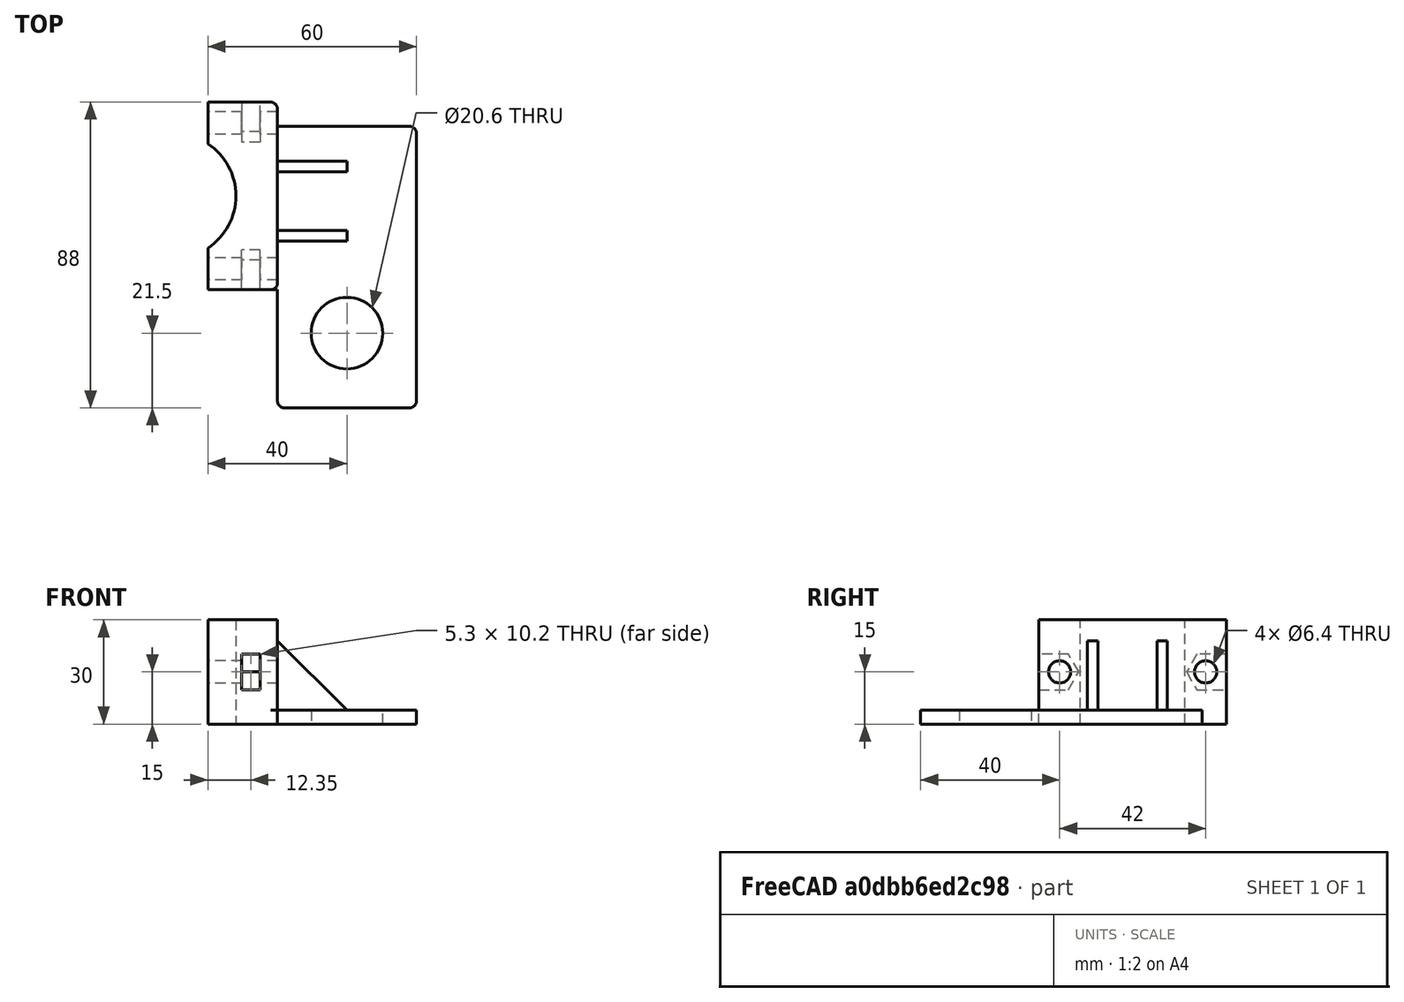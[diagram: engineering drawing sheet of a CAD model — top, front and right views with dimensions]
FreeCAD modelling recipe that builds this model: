
FCSTD DOCUMENT  (FreeCAD 0.18R16117 (Git))
Label: encloser_halter_v2
License: All rights reserved
LicenseURL: http://en.wikipedia.org/wiki/All_rights_reserved
objects: TechDraw::DrawViewDimension×8, Sketcher::SketchObject×4, Part::Extrusion×4, Part::FeaturePython×3, TechDraw::DrawProjGroupItem×3, Part::MultiFuse×2, Part::Cylinder×1, Part::Fillet×1, Part::Cut×1, TechDraw::DrawSVGTemplate×1, TechDraw::DrawProjGroup×1, TechDraw::DrawPage×1
note: 16 computed .brp shape members not serialized (recipe doc carries the construction recipe); baked Part::Feature solids carry a one-line shape summary decoded from their .brp

FEATURE [Sketcher::SketchObject] Sketch
  sketch-geometry (9):
    g0: LineSegment StartX=38 StartY=0 StartZ=0 EndX=2 EndY=0 EndZ=0
    g1: LineSegment StartX=0 StartY=2 StartZ=0 EndX=0 EndY=81 EndZ=0
    g2: LineSegment StartX=0 StartY=81 StartZ=0 EndX=38 EndY=81 EndZ=0
    g3: LineSegment StartX=40 StartY=79 StartZ=0 EndX=40 EndY=2 EndZ=0
    g4: Circle CenterX=20 CenterY=21.5 CenterZ=0 NormalX=0 NormalY=0 NormalZ=1 AngleXU=0 Radius=10.3
    g5: LineSegment [constr] StartX=20 StartY=0 StartZ=0 EndX=20 EndY=81 EndZ=0
    g6: ArcOfCircle CenterX=38 CenterY=79 CenterZ=0 NormalX=0 NormalY=0 NormalZ=1 AngleXU=0 Radius=2 StartAngle=-9e-16 EndAngle=1.5708
    g7: ArcOfCircle CenterX=38 CenterY=2 CenterZ=0 NormalX=0 NormalY=0 NormalZ=1 AngleXU=0 Radius=2 StartAngle=4.71239 EndAngle=6.28319
    g8: ArcOfCircle CenterX=2 CenterY=2 CenterZ=0 NormalX=0 NormalY=0 NormalZ=1 AngleXU=0 Radius=2 StartAngle=3.14159 EndAngle=4.71239
  constraints (24):
    c: Coincident(g1,g2)
    c: Horizontal(g0)
    c: Horizontal(g2)
    c: Vertical(g1)
    c: Vertical(g3)
    c: Radius(g4) = 10.3
    c: PointOnObject(g5,g0)
    c: PointOnObject(g4,g5)
    c: DistanceY(g-1,g4) = 21.5
    c: PointOnObject(g5,g2)
    c: Tangent(g2,g6) = 1.5708
    c: Tangent(g3,g6) = 1.5708
    c: Tangent(g3,g7) = 1.5708
    c: Tangent(g0,g7) = 1.5708
    c: Tangent(g1,g8) = 1.5708
    c: Tangent(g0,g8) = 1.5708
    c: Radius(g8) = 2
    c: Equal(g8,g7)
    c: Equal(g8,g6)
    c: DistanceX(g1,g3) = 40
    c: PointOnObject(g1,g-2)
    c: PointOnObject(g0,g-1)
    c: DistanceY(g0,g2) = 81
    c: Symmetric(g1,g3,g5)
FEATURE [Part::Extrusion] Extrude  label="encloser_mount_plate"
  Base = -> Sketch
  Dir = (0,0,1)
  DirMode = 2
  FaceMakerClass = Part::FaceMakerBullseye
  LengthFwd = 4
  LengthRev = 0
  Placement = pos=(0,-61,0) rot=(0,0,1;0rad)
  Solid = true
  Symmetric = false
FEATURE [Sketcher::SketchObject] Sketch002  label="Sketch_encloser_mastbefestigung"
  sketch-geometry (6):
    g0: LineSegment StartX=-20 StartY=27 StartZ=0 EndX=0 EndY=27 EndZ=0
    g1: LineSegment StartX=0 StartY=27 StartZ=0 EndX=0 EndY=-27 EndZ=0
    g2: LineSegment StartX=0 StartY=-27 StartZ=0 EndX=-20 EndY=-27 EndZ=0
    g3: LineSegment StartX=-20 StartY=-27 StartZ=0 EndX=-20 EndY=-15 EndZ=0
    g4: LineSegment StartX=-20 StartY=15 StartZ=0 EndX=-20 EndY=27 EndZ=0
    g5: ArcOfCircle CenterX=-29.9499 CenterY=2e-16 CenterZ=0 NormalX=0 NormalY=0 NormalZ=1 AngleXU=0 Radius=18 StartAngle=5.29807 EndAngle=7.2683
  constraints (17):
    c: Horizontal(g0)
    c: Horizontal(g2)
    c: Coincident(g2,g3)
    c: Vertical(g3)
    c: Coincident(g4,g0)
    c: Vertical(g4)
    c: Coincident(g5,g4)
    c: Coincident(g5,g3)
    c: DistanceY(g3,g3) = 12
    c: Symmetric(g3,g4,g-1)
    c: DistanceY(g2,g0) = 54
    c: PointOnObject(g1,g-2)
    c: DistanceX(g2,g1) = 20
    c: Symmetric(g2,g0,g-1)
    c: Coincident(g0,g1)
    c: Coincident(g2,g1)
    c: Radius(g5) = 18
FEATURE [Part::Extrusion] Extrude002  label="encloser_mastbefestigung"
  Base = -> Sketch002
  Dir = (0,0,1)
  DirMode = 2
  FaceMakerClass = Part::FaceMakerBullseye
  LengthFwd = 30
  LengthRev = 0
  Solid = true
  Symmetric = false
FEATURE [Part::Cylinder] Cylinder  label="Bohrung"
  Angle = 360
  AttacherType = Attacher::AttachEngine3D
  Height = 30
  Placement = pos=(0,-21,15) rot=(0,-1,0;1.5708rad)
  Radius = 3.2
FEATURE [Part::FeaturePython] Clone  label="Bohrung001"  # Draft clone (typed FeaturePython)
  AttacherType = Attacher::AttachEngine3D
  Fuse = false
  Objects = -> [Cylinder]
  Placement = pos=(0,21,15) rot=(0,-1,0;1.5708rad)
  Scale = (1,1,1)
FEATURE [Sketcher::SketchObject] Sketch003  label="Sketch_Winkel"
  ExternalGeometry = -> [Extrude002,Extrude]
  Placement = pos=(0,0,0) rot=(1,0,0;1.5708rad)
  sketch-geometry (3):
    g0: LineSegment StartX=0 StartY=24 StartZ=0 EndX=20 EndY=4 EndZ=0
    g1: LineSegment StartX=20 StartY=4 StartZ=0 EndX=0 EndY=4 EndZ=0
    g2: LineSegment StartX=0 StartY=4 StartZ=0 EndX=0 EndY=24 EndZ=0
  constraints (9):
    c: PointOnObject(g0,g-3)
    c: PointOnObject(g0,g-4)
    c: Coincident(g0,g1)
    c: PointOnObject(g1,g-3)
    c: Horizontal(g1)
    c: Coincident(g1,g2)
    c: Coincident(g2,g0)
    c: DistanceX(g1,g1) = 20
    c: DistanceY(g2,g2) = 20
FEATURE [Part::Extrusion] Extrude003  label="Winkel"
  Base = -> Sketch003
  Dir = (0,-1,2e-16)
  DirMode = 2
  FaceMakerClass = Part::FaceMakerBullseye
  LengthFwd = 3
  LengthRev = 0
  Placement = pos=(0,-10,0) rot=(0,0,1;0rad)
  Solid = true
  Symmetric = false
FEATURE [Part::FeaturePython] Clone001  label="Winkel001"  # Draft clone (typed FeaturePython)
  AttacherType = Attacher::AttachEngine3D
  Fuse = false
  Objects = -> [Extrude003]
  Placement = pos=(0,10,0) rot=(0,0,1;0rad)
  Scale = (1,1,1)
FEATURE [Part::MultiFuse] Fusion001  label="encloser_halter_roh"
  Shapes = -> [Extrude,Extrude002,Extrude003,Clone001]
FEATURE [Part::Fillet] Fillet  label="encloser_halter_gerundet"
  Base = -> Fusion001
  Edges = 2 edges r=2: [Edge48,Edge50]
FEATURE [Sketcher::SketchObject] Sketch004  label="Sketch_Ausschnitt_M6"
  Placement = pos=(0,0,0) rot=(0.57735,-0.57735,-0.57735;2.0944rad)
  sketch-geometry (6):
    g0: LineSegment StartX=15.5 StartY=15 StartZ=0 EndX=18.4445 EndY=20.1 EndZ=0
    g1: LineSegment StartX=18.4445 StartY=20.1 StartZ=0 EndX=30.4445 EndY=20.1 EndZ=0
    g2: LineSegment StartX=30.4445 StartY=20.1 StartZ=0 EndX=30.4445 EndY=9.9 EndZ=0
    g3: LineSegment StartX=30.4445 StartY=9.9 StartZ=0 EndX=18.4445 EndY=9.9 EndZ=0
    g4: LineSegment StartX=18.4445 StartY=9.9 StartZ=0 EndX=15.5 EndY=15 EndZ=0
    g5: LineSegment [constr] StartX=30.4445 StartY=15 StartZ=0 EndX=15.5 EndY=15 EndZ=0
  constraints (14):
    c: Coincident(g0,g1)
    c: Horizontal(g1)
    c: Coincident(g1,g2)
    c: Vertical(g2)
    c: Coincident(g2,g3)
    c: Coincident(g3,g4)
    c: Coincident(g4,g0)
    c: DistanceY(g2,g2) = 10.2
    c: PointOnObject(g5,g2)
    c: Coincident(g5,g0)
    c: Symmetric(g1,g2,g5)
    c: Symmetric(g3,g0,g5)
    c: Angle(g4,g0) = 2.0944
    c: DistanceX(g1,g1) = 12
FEATURE [Part::Extrusion] Extrude004  label="Ausschnitt_M6"
  Base = -> Sketch004
  Dir = (-1,0,0)
  DirMode = 2
  FaceMakerClass = Part::FaceMakerBullseye
  LengthFwd = 5.3
  LengthRev = 0
  Placement = pos=(-5,0,0) rot=(0,0,1;0rad)
  Solid = true
  Symmetric = false
FEATURE [Part::FeaturePython] Clone002  label="Ausschnitt_M007"  # Draft clone (typed FeaturePython)
  AttacherType = Attacher::AttachEngine3D
  Fuse = false
  Objects = -> [Extrude004]
  Placement = pos=(-5,0,30) rot=(1,0,0;3.14159rad)
  Scale = (1,1,1)
FEATURE [Part::MultiFuse] Fusion  label="Ausschnitte"
  Shapes = -> [Cylinder,Clone,Clone002,Extrude004]
FEATURE [Part::Cut] Cut  label="encloser_halter"
  Base = -> Fillet
  Tool = -> Fusion
FEATURE [TechDraw::DrawSVGTemplate] Template
  EditableTexts = Designed_by_Name=W.Klenner; FC-Date=04.03.2020; FC-SC=1:1; FC-SH=1; FC-Title=Energy Harvester; Subtitle=Gehäuse Halter
  Height = 210
  Orientation = 1
  Width = 297
FEATURE [TechDraw::DrawProjGroupItem] ProjItem  label="Front"
  CoarseView = false
  Direction = (0,0,1)
  Focus = 100
  HardHidden = false
  IsoCount = 0
  IsoHidden = false
  IsoVisible = false
  LockPosition = true
  Perspective = false
  Rotation = 0
  RotationVector = (1,0,0)
  ScaleType = 2
  SeamHidden = false
  SeamVisible = false
  SmoothHidden = false
  SmoothVisible = false
  Source = -> [Cut]
  Type = 0
  X = 0
  Y = 0
FEATURE [TechDraw::DrawProjGroupItem] ProjItem001  label="Right"
  CoarseView = false
  Direction = (1,0,1e-16)
  Focus = 100
  HardHidden = false
  IsoCount = 0
  IsoHidden = false
  IsoVisible = false
  LockPosition = false
  Perspective = false
  Rotation = 0
  RotationVector = (1e-16,0,-1)
  ScaleType = 2
  SeamHidden = false
  SeamVisible = false
  SmoothHidden = false
  SmoothVisible = false
  Source = -> [Cut]
  Type = 2
  X = 97.2208
  Y = 0
FEATURE [TechDraw::DrawProjGroupItem] ProjItem002  label="Top"
  CoarseView = false
  Direction = (0,1,0)
  Focus = 100
  HardHidden = false
  IsoCount = 0
  IsoHidden = false
  IsoVisible = false
  LockPosition = false
  Perspective = false
  Rotation = 0
  RotationVector = (1,0,0)
  ScaleType = 2
  SeamHidden = false
  SeamVisible = false
  SmoothHidden = false
  SmoothVisible = false
  Source = -> [Cut]
  Type = 4
  X = 0
  Y = -99.0918
FEATURE [TechDraw::DrawProjGroup] ProjGroup
  Anchor = -> ProjItem
  AutoDistribute = false
  LockPosition = false
  ProjectionType = 0
  Rotation = 0
  ScaleType = 0
  Source = -> [Cut]
  Views = -> [ProjItem,ProjItem001,ProjItem002]
  X = 91.9615
  Y = 137.047
  spacingX = 15
  spacingY = 15
FEATURE [TechDraw::DrawViewDimension] Dimension
  Arbitrary = false
  FormatSpec = %.2f
  LockPosition = false
  MeasureType = 1
  OverTolerance = 0
  References2D = -> [ProjItem]
  Rotation = 0
  ScaleType = 0
  Type = 1
  UnderTolerance = 0
  X = 9.73945
  Y = -58.9355
FEATURE [TechDraw::DrawViewDimension] Dimension001
  Arbitrary = false
  FormatSpec = %.2f
  LockPosition = false
  MeasureType = 1
  OverTolerance = 0
  References2D = -> [ProjItem]
  Rotation = 0
  ScaleType = 0
  Type = 2
  UnderTolerance = 0
  X = 38.4218
  Y = -3.23945
FEATURE [TechDraw::DrawViewDimension] Dimension002
  Arbitrary = false
  FormatSpec = ⌀%.2f
  LockPosition = false
  MeasureType = 1
  OverTolerance = 0
  References2D = -> [ProjItem]
  Rotation = 0
  ScaleType = 0
  Type = 5
  UnderTolerance = 0
  X = 15.3722
  Y = -36.737
FEATURE [TechDraw::DrawViewDimension] Dimension004
  Arbitrary = false
  FormatSpec = ⌀%.2f
  LockPosition = false
  MeasureType = 1
  OverTolerance = 0
  References2D = -> [ProjItem]
  Rotation = 0
  ScaleType = 0
  Type = 5
  UnderTolerance = 0
  X = -47.6799
  Y = 15.3722
FEATURE [TechDraw::DrawViewDimension] Dimension005
  Arbitrary = false
  FormatSpec = %.2f
  LockPosition = false
  MeasureType = 1
  OverTolerance = 0
  References2D = -> [ProjItem001]
  Rotation = 0
  ScaleType = 0
  Type = 1
  UnderTolerance = 0
  X = -1.82382
  Y = 51.3797
FEATURE [TechDraw::DrawViewDimension] Dimension006
  Arbitrary = false
  FormatSpec = %.2f
  LockPosition = false
  MeasureType = 1
  OverTolerance = 0
  References2D = -> [ProjItem001]
  Rotation = 0
  ScaleType = 0
  Type = 2
  UnderTolerance = 0
  X = -33.0893
  Y = 16.7395
FEATURE [TechDraw::DrawViewDimension] Dimension007
  Arbitrary = false
  FormatSpec = %.2f
  LockPosition = false
  MeasureType = 1
  OverTolerance = 0
  References2D = -> [ProjItem002]
  Rotation = 0
  ScaleType = 0
  Type = 2
  UnderTolerance = 0
  X = 37.0347
  Y = 3.3598
FEATURE [TechDraw::DrawViewDimension] Dimension008
  Arbitrary = false
  FormatSpec = %.2f
  LockPosition = false
  MeasureType = 1
  OverTolerance = 0
  References2D = -> [ProjItem]
  Rotation = 0
  ScaleType = 0
  Type = 1
  UnderTolerance = 0
  X = -18.6973
  Y = 55.7097
FEATURE [TechDraw::DrawPage] Page
  KeepUpdated = true
  ProjectionType = 0
  Template = -> Template
  Views = -> [ProjGroup,Dimension,Dimension001,Dimension002,Dimension004,Dimension005,Dimension006,Dimension007,Dimension008]
